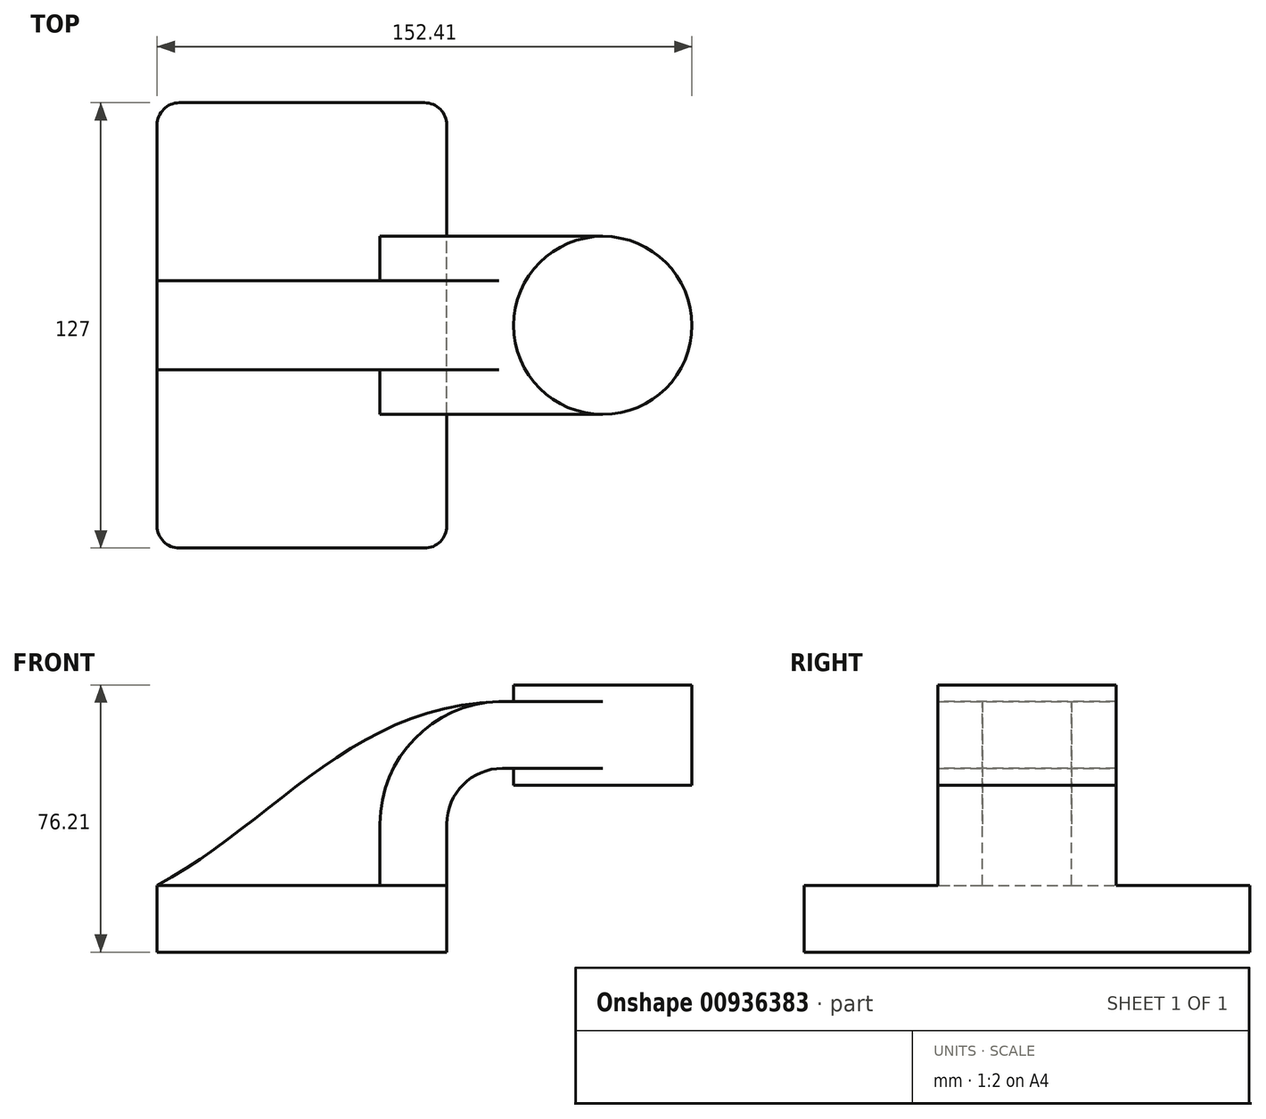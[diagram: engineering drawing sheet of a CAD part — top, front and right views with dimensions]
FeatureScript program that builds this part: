
annotation { "Feature Type Name" : "Feature", "Feature Type Description" : "" }
export const myFeature = defineFeature(function(context is Context, id is Id, definition is map)
    precondition{}
    {
        {
            var Q0;
            Q0=qCreatedBy(makeId("Front.planeOp"),FACE);
            var sketch = newSketch(context, id + "F0", { "sketchPlane" : qUnion([Q0])});
            skLineSegment(sketch, "E0.bottom", {"start": v(41.27, 9.53) * mm, "end": v(-41.28, 9.53) * mm});
            skLineSegment(sketch, "E0.top", {"start": v(41.28, -9.52) * mm, "end": v(-41.27, -9.52) * mm});
            skLineSegment(sketch, "E0.left", {"start": v(41.28, 9.53) * mm, "end": v(41.28, -9.52) * mm});
            skLineSegment(sketch, "E0.right", {"start": v(-41.28, 9.53) * mm, "end": v(-41.27, -9.52) * mm});
            skPoint(sketch, "E0.middle", {"position": v(0, 0) * mm});
            skPoint(sketch, "E1.middle", {"position": v(85.72, 52.39) * mm});
            skLineSegment(sketch, "E2", {"start": v(41.27, 9.53) * mm, "end": v(41.27, 27) * mm});
            skArc(sketch, "E3", {"start": v(41.27, 27) * mm, "mid": v(45.92, 38.23) * mm, "end": v(57.15, 42.88) * mm});
            skLineSegment(sketch, "E4", {"start": v(57.15, 42.88) * mm, "end": v(85.72, 42.88) * mm});
            skFitSpline(sketch, "E5", {"points": [v(-41.28, 9.53) * mm, v(57.15, 61.93) * mm], "startDerivative": vector(98.43, 52.15) * mm, "endDerivative": vector(127.41, 1.1) * mm});
            skLineSegment(sketch, "E6.bottom", {"start": v(111.13, 38.1) * mm, "end": v(60.33, 38.1) * mm});
            skLineSegment(sketch, "E6.top", {"start": v(111.13, 66.68) * mm, "end": v(60.33, 66.68) * mm});
            skLineSegment(sketch, "E6.left", {"start": v(111.13, 38.1) * mm, "end": v(111.13, 66.68) * mm});
            skLineSegment(sketch, "E6.right", {"start": v(60.33, 38.1) * mm, "end": v(60.33, 66.68) * mm});
            skPoint(sketch, "E6.middle", {"position": v(85.73, 52.39) * mm});
            skLineSegment(sketch, "E7.0", {"start": v(57.15, 61.93) * mm, "end": v(85.72, 61.93) * mm});
            skArc(sketch, "E7.1", {"start": v(22.23, 27) * mm, "mid": v(32.45, 51.7) * mm, "end": v(57.15, 61.93) * mm});
            skLineSegment(sketch, "E7.2", {"start": v(22.22, 9.53) * mm, "end": v(22.22, 27) * mm});
            skLineSegment(sketch, "E8", {"start": v(85.73, 66.68) * mm, "end": v(85.73, 38.1) * mm});
            skSolve(sketch);
        }
        {
            var Q0;
            Q0=makeQuery(id+"F0.imprint","IMPRINT",FACE,{"disambiguationData":[TD([[makeQuery(id+"F0.imprint","IMPRINT",EDGE,{"derivedFrom":sQuery(id+"F0.wireOp",EDGE,"E0.top")}),-1.0]])]});
            extrude(context, id + "F1", {"entities" : qUnion([Q0]), "depth" : 127 * mm, "offsetDistance" : 25.4 * mm, "symmetric" : true});
        }
        {
            var Q0;
            {var subQ6=sQuery(id+"F0.wireOp",EDGE,"E2");Q0=makeQuery(id+"F0.imprint","IMPRINT",FACE,{"disambiguationData":[TD([[makeQuery(id+"F0.imprint","IMPRINT",EDGE,{"derivedFrom":subQ6}),1.0]])]});}
            extrude(context, id + "F2", {"entities" : qUnion([Q0]), "operationType" : NewBodyOperationType.ADD, "depth" : 50.8 * mm, "offsetDistance" : 25.4 * mm, "symmetric" : true});
        }
        {
            var Q0;
            {var subQ3=sQuery(id+"F0.wireOp",EDGE,"E7.2");Q0=makeQuery(id+"F0.imprint","IMPRINT",FACE,{"disambiguationData":[TD([[makeQuery(id+"F0.imprint","IMPRINT",EDGE,{"derivedFrom":subQ3}),1.0]])]});}
            extrude(context, id + "F3", {"entities" : qUnion([Q0]), "operationType" : NewBodyOperationType.ADD, "depth" : 25.4 * mm, "offsetDistance" : 25.4 * mm, "symmetric" : true});
        }
        {
            var Q0;
            {var subQ0=sQuery(id+"F0.wireOp",EDGE,"E8");var subQ1=sQuery(id+"F0.wireOp",EDGE,"E4");var subQ2=makeQuery(id+"F0.imprint","INTERSECT",VERTEX,{"derivedFrom":[subQ1,subQ0]});Q0=makeQuery(id+"F0.imprint","IMPRINT",FACE,{"disambiguationData":[TD([[makeQuery(id+"F0.imprint","IMPRINT",EDGE,{"disambiguationData":[TD([[subQ2,1.0]])],"derivedFrom":subQ1}),1.0]])]});}
            extrude(context, id + "F4", {"entities" : qUnion([Q0]), "operationType" : NewBodyOperationType.ADD, "depth" : 50.8 * mm, "offsetDistance" : 25.4 * mm, "symmetric" : true});
        }
        {
            var Q0;
            {var subQ4=sQuery(id+"F0.wireOp",EDGE,"E6.left");Q0=makeQuery(id+"F0.imprint","IMPRINT",FACE,{"disambiguationData":[TD([[makeQuery(id+"F0.imprint","IMPRINT",EDGE,{"derivedFrom":subQ4}),1.0]])]});}
            var Q1;
            Q1=sQuery(id+"F0.wireOp",EDGE,"E8");
            revolve(context, id + "F5", {"operationType" : NewBodyOperationType.ADD, "surfaceOperationType" : NewSurfaceOperationType.NEW, "entities" : qUnion([Q0]), "axis" : qUnion([Q1]), "revolveType" : RevolveType.FULL});
        }
        {
            var Q0;
            Q0=makeQuery(id+"F1.opExtrude","CAP_EDGE",EDGE,{"disambiguationData":[OSD([sQuery(id+"F0.wireOp",EDGE,"E0.left")])],"isStart":false});
            var Q1;
            Q1=makeQuery(id+"F1.opExtrude","CAP_EDGE",EDGE,{"disambiguationData":[OSD([sQuery(id+"F0.wireOp",EDGE,"E0.right")])],"isStart":false});
            var Q2;
            Q2=makeQuery(id+"F1.opExtrude","CAP_EDGE",EDGE,{"disambiguationData":[OSD([sQuery(id+"F0.wireOp",EDGE,"E0.right")])],"isStart":true});
            var Q3;
            Q3=makeQuery(id+"F1.opExtrude","CAP_EDGE",EDGE,{"disambiguationData":[OSD([sQuery(id+"F0.wireOp",EDGE,"E0.left")])],"isStart":true});
            fillet(context, id + "F6", {"entities" : qUnion([Q0, Q1, Q2, Q3]), "radius" : 6.35 * mm, "tangentPropagation" : true, "allowEdgeOverflow" : false});
        }
    });
